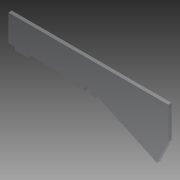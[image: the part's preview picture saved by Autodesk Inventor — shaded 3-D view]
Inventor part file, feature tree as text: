
AUTODESK INVENTOR PART (.ipt)
format: ipt  version: 2013 (Build 170138000, 138)  size: 111,104 bytes
history: native  units: in
note: dims shown in document units (in); Inventor stores cm internally (conversion verified against a paired STEP export)
features: reference x5, extrude x2, sketch x2
ambient origin geometry x8: Origin, YZ Plane, XZ Plane, XY Plane, X Axis, Y Axis, Z Axis, Center Point
bodies: Solid1 (feature_tree)
feature tree (9):
  extrude  "Extrusion1"  Depth=3.125in
  extrude  "Extrusion2"  Depth=0.125in
  sketch  "Sketch1"  dims[d0=1.0in d1=3.125in]
  sketch  "Sketch2"  dims[d2=0.25in d4=0.125in d5=0.5in d6=0.25in d7=0.125in d8=0.5in d9=1.0in d10=1.0in d11=0.125in d12=0.0in d13=1.0in d14=0.125in d15=0.0in]
  reference  "Reference1"
  reference  "Reference2"
  reference  "Reference3"
  reference  "Reference4"
  reference  "Reference5"
